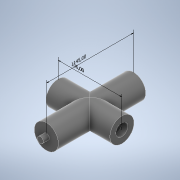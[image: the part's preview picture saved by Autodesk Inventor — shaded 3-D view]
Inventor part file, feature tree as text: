
AUTODESK INVENTOR PART (.ipt)
format: ipt  version: 2021 (Build 250183000, 183)  size: 145,408 bytes
history: native  units: mm
features: extrude x6, sketch x6, other x3
ambient origin geometry x8: Origin, YZ Plane, XZ Plane, XY Plane, X Axis, Y Axis, Z Axis, Center Point
bodies: Solid1 (feature_tree)
feature tree (15):
  other  "Annotations"
  extrude  "Extrusion1"  Depth=106.0mm TaperAngle=0.0deg
  extrude  "Extrusion2"  Depth=10.0mm TaperAngle=0.0deg
  extrude  "Extrusion3"  Depth=10.0mm TaperAngle=0.0deg
  extrude  "Extrusion4"  Depth=10.0mm
  extrude  "Extrusion5"  Depth=10.0mm TaperAngle=0.0deg
  extrude  "Extrusion6"  [1 undecoded]
  sketch  "Sketch1"  dims[d0=40.0mm d1=106.0mm d2=0.0mm]
  sketch  "Sketch2"  dims[d3=20.0mm d4=10.0mm d5=0.0mm]
  sketch  "Sketch3"  dims[d6=20.0mm d7=10.0mm d8=0.0mm]
  sketch  "Sketch5"  dims[d10=145.0mm d11=0.0mm d12=10.0mm]
  sketch  "Sketch6"  dims[d13=10.0mm d14=0.0mm d15=10.0mm d16=0.0mm]
  sketch  "Sketch7"  dims[d17=145.0mm d18=106.0mm]
  other  "Linear Dimension 1"
  other  "Linear Dimension 2"
note: 1 required parameter value undecoded (feature->parameter linkage not recoverable at this tier; creation-order binding heuristic only, values carry confidence <= 0.55)
